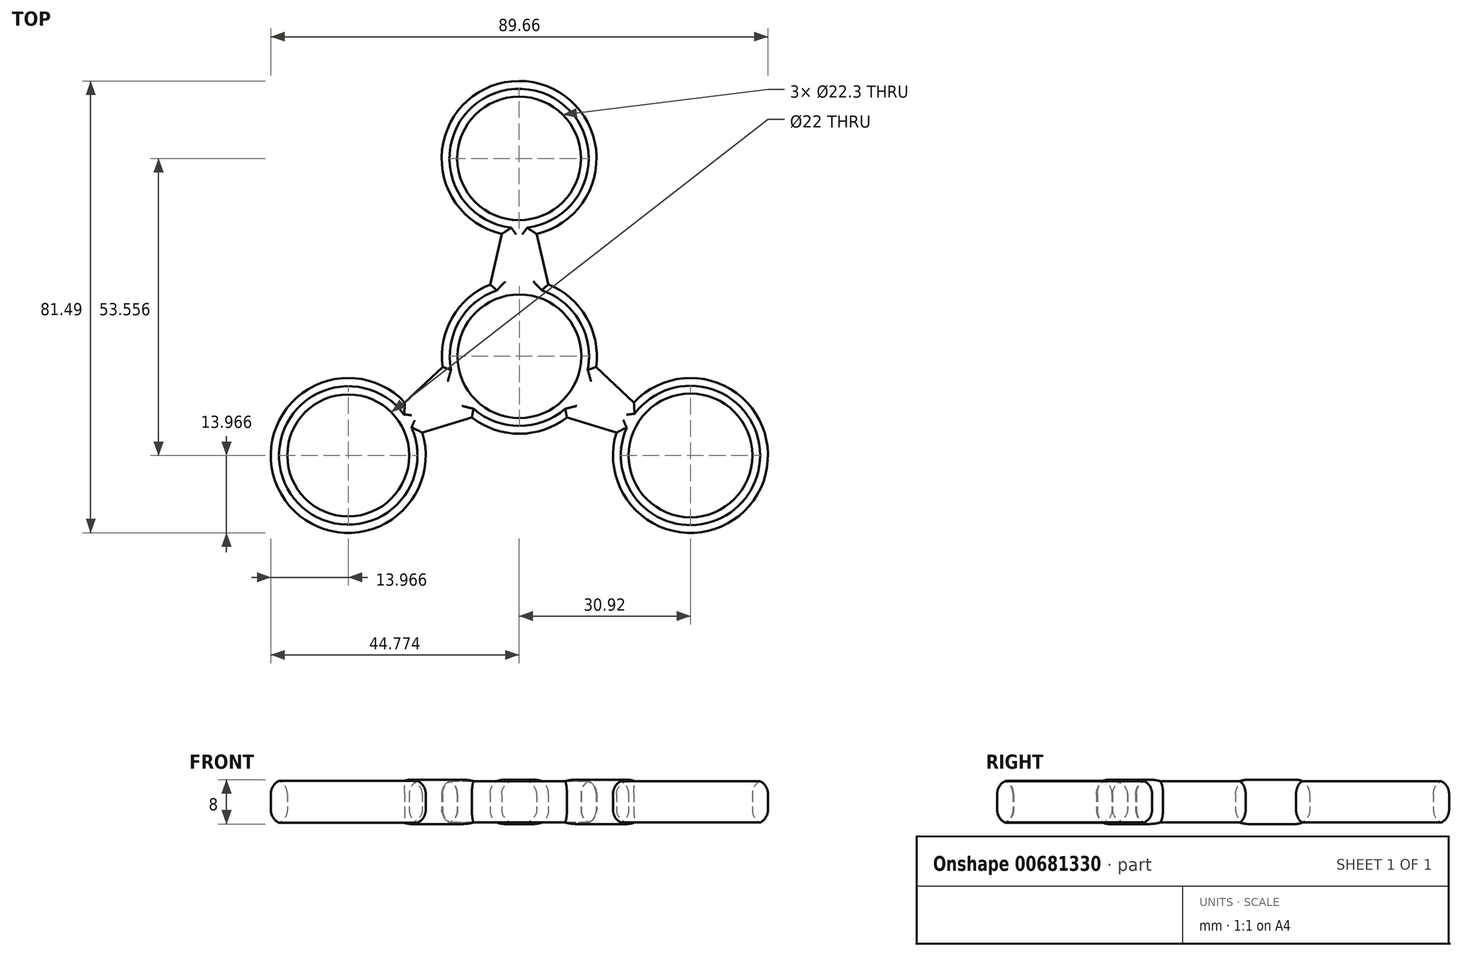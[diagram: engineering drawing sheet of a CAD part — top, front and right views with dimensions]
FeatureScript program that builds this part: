
annotation { "Feature Type Name" : "Feature", "Feature Type Description" : "" }
export const myFeature = defineFeature(function(context is Context, id is Id, definition is map)
    precondition{}
    {
        {
            var Q0;
            Q0=qCreatedBy(makeId("Top.planeOp"),FACE);
            var sketch = newSketch(context, id + "F0", { "sketchPlane" : qUnion([Q0])});
            skPoint(sketch, "E0.0.midPoint", {"position": v(30.86, 17.88) * mm});
            skLineSegment(sketch, "E1", {"start": v(0, 0) * mm, "end": v(-0.11, 71.34) * mm});
            skLineSegment(sketch, "E2", {"start": v(0, 0) * mm, "end": v(61.84, -35.57) * mm});
            skLineSegment(sketch, "E3", {"start": v(0, 0) * mm, "end": v(-61.73, -35.77) * mm});
            skCircle(sketch, "E4", {"center": v(-0.06, 35.67) * mm, "radius": 11.15 * mm});
            skCircle(sketch, "E5", {"center": v(30.86, -17.88) * mm, "radius": 11.15 * mm});
            skCircle(sketch, "E6", {"center": v(-30.86, -17.88) * mm, "radius": 11 * mm});
            skLineSegment(sketch, "E7", {"start": v(-30.86, -17.88) * mm, "end": v(0, -8.4) * mm});
            skLineSegment(sketch, "E8", {"start": v(0, -8.4) * mm, "end": v(30.86, -17.88) * mm});
            skLineSegment(sketch, "E9", {"start": v(0, 0) * mm, "end": v(7.27, 4.22) * mm});
            skLineSegment(sketch, "E10", {"start": v(0, -8.4) * mm, "end": v(0, 0) * mm});
            skLineSegment(sketch, "E11", {"start": v(-0.06, 35.67) * mm, "end": v(7.27, 4.22) * mm});
            skLineSegment(sketch, "E12", {"start": v(7.27, 4.22) * mm, "end": v(30.86, -17.88) * mm});
            skLineSegment(sketch, "E13", {"start": v(0, 0) * mm, "end": v(-7.29, 4.2) * mm});
            skLineSegment(sketch, "E14", {"start": v(-0.06, 35.67) * mm, "end": v(-7.29, 4.2) * mm});
            skLineSegment(sketch, "E15", {"start": v(-7.29, 4.2) * mm, "end": v(-30.86, -17.88) * mm});
            skCircle(sketch, "E16", {"center": v(0, 0) * mm, "radius": 11.15 * mm});
            skCircle(sketch, "E17", {"center": v(-30.86, -17.88) * mm, "radius": 13.97 * mm});
            skCircle(sketch, "E18", {"center": v(30.86, -17.88) * mm, "radius": 13.97 * mm});
            skCircle(sketch, "E19", {"center": v(-0.06, 35.67) * mm, "radius": 13.97 * mm});
            skCircle(sketch, "E20", {"center": v(0, 0) * mm, "radius": 13.97 * mm});
            skSolve(sketch);
        }
        {
            var Q0;
            {var subQ0=sQuery(id+"F0.wireOp",EDGE,"E19");var subQ1=sQuery(id+"F0.wireOp",EDGE,"E1");var subQ2=makeQuery(id+"F0.imprint","INTERSECT",VERTEX,{"disambiguationData":[OD(0.0)],"derivedFrom":[subQ1,subQ0]});Q0=makeQuery(id+"F0.imprint","IMPRINT",FACE,{"disambiguationData":[TD([[makeQuery(id+"F0.imprint","IMPRINT",EDGE,{"disambiguationData":[TD([[subQ2,1.0]])],"derivedFrom":subQ1}),-1.0]])]});}
            var Q1;
            {var subQ0=sQuery(id+"F0.wireOp",EDGE,"E19");var subQ1=sQuery(id+"F0.wireOp",EDGE,"E1");var subQ2=makeQuery(id+"F0.imprint","INTERSECT",VERTEX,{"disambiguationData":[OD(0.0)],"derivedFrom":[subQ1,subQ0]});Q1=makeQuery(id+"F0.imprint","IMPRINT",FACE,{"disambiguationData":[TD([[makeQuery(id+"F0.imprint","IMPRINT",EDGE,{"disambiguationData":[TD([[subQ2,1.0]])],"derivedFrom":subQ1}),1.0]])]});}
            var Q2;
            {var subQ0=sQuery(id+"F0.wireOp",EDGE,"E20");var subQ1=sQuery(id+"F0.wireOp",EDGE,"E1");var subQ2=makeQuery(id+"F0.imprint","INTERSECT",VERTEX,{"derivedFrom":[subQ1,subQ0]});Q2=makeQuery(id+"F0.imprint","IMPRINT",FACE,{"disambiguationData":[TD([[makeQuery(id+"F0.imprint","IMPRINT",EDGE,{"disambiguationData":[TD([[subQ2,-1.0]])],"derivedFrom":subQ1}),1.0]])]});}
            var Q3;
            {var subQ0=sQuery(id+"F0.wireOp",EDGE,"E20");var subQ1=sQuery(id+"F0.wireOp",EDGE,"E1");var subQ2=makeQuery(id+"F0.imprint","INTERSECT",VERTEX,{"derivedFrom":[subQ1,subQ0]});Q3=makeQuery(id+"F0.imprint","IMPRINT",FACE,{"disambiguationData":[TD([[makeQuery(id+"F0.imprint","IMPRINT",EDGE,{"disambiguationData":[TD([[subQ2,-1.0]])],"derivedFrom":subQ1}),-1.0]])]});}
            var Q4;
            {var subQ0=sQuery(id+"F0.wireOp",EDGE,"E19");var subQ1=sQuery(id+"F0.wireOp",EDGE,"E1");var subQ2=makeQuery(id+"F0.imprint","INTERSECT",VERTEX,{"disambiguationData":[OD(1.0)],"derivedFrom":[subQ1,subQ0]});Q4=makeQuery(id+"F0.imprint","IMPRINT",FACE,{"disambiguationData":[TD([[makeQuery(id+"F0.imprint","IMPRINT",EDGE,{"disambiguationData":[TD([[subQ2,-1.0]])],"derivedFrom":subQ1}),-1.0]])]});}
            var Q5;
            {var subQ0=sQuery(id+"F0.wireOp",EDGE,"E19");var subQ1=sQuery(id+"F0.wireOp",EDGE,"E1");var subQ2=makeQuery(id+"F0.imprint","INTERSECT",VERTEX,{"disambiguationData":[OD(1.0)],"derivedFrom":[subQ1,subQ0]});Q5=makeQuery(id+"F0.imprint","IMPRINT",FACE,{"disambiguationData":[TD([[makeQuery(id+"F0.imprint","IMPRINT",EDGE,{"disambiguationData":[TD([[subQ2,-1.0]])],"derivedFrom":subQ1}),1.0]])]});}
            var Q6;
            {var subQ0=sQuery(id+"F0.wireOp",EDGE,"E20");var subQ1=sQuery(id+"F0.wireOp",EDGE,"E11");var subQ2=makeQuery(id+"F0.imprint","INTERSECT",VERTEX,{"derivedFrom":[subQ1,subQ0]});Q6=makeQuery(id+"F0.imprint","IMPRINT",FACE,{"disambiguationData":[TD([[makeQuery(id+"F0.imprint","IMPRINT",EDGE,{"disambiguationData":[TD([[subQ2,-1.0]])],"derivedFrom":subQ1}),1.0]])]});}
            var Q7;
            {var subQ0=sQuery(id+"F0.wireOp",EDGE,"E20");var subQ1=sQuery(id+"F0.wireOp",EDGE,"E14");var subQ2=makeQuery(id+"F0.imprint","INTERSECT",VERTEX,{"derivedFrom":[subQ1,subQ0]});Q7=makeQuery(id+"F0.imprint","IMPRINT",FACE,{"disambiguationData":[TD([[makeQuery(id+"F0.imprint","IMPRINT",EDGE,{"disambiguationData":[TD([[subQ2,-1.0]])],"derivedFrom":subQ1}),-1.0]])]});}
            var Q8;
            {var subQ0=sQuery(id+"F0.wireOp",EDGE,"E16");var subQ1=sQuery(id+"F0.wireOp",EDGE,"E1");var subQ2=makeQuery(id+"F0.imprint","INTERSECT",VERTEX,{"derivedFrom":[subQ1,subQ0]});Q8=makeQuery(id+"F0.imprint","IMPRINT",FACE,{"disambiguationData":[TD([[makeQuery(id+"F0.imprint","IMPRINT",EDGE,{"disambiguationData":[TD([[subQ2,-1.0]])],"derivedFrom":subQ1}),-1.0]])]});}
            var Q9;
            {var subQ0=sQuery(id+"F0.wireOp",EDGE,"E16");var subQ1=sQuery(id+"F0.wireOp",EDGE,"E1");var subQ2=makeQuery(id+"F0.imprint","INTERSECT",VERTEX,{"derivedFrom":[subQ1,subQ0]});Q9=makeQuery(id+"F0.imprint","IMPRINT",FACE,{"disambiguationData":[TD([[makeQuery(id+"F0.imprint","IMPRINT",EDGE,{"disambiguationData":[TD([[subQ2,-1.0]])],"derivedFrom":subQ1}),1.0]])]});}
            var Q10;
            {var subQ0=sQuery(id+"F0.wireOp",EDGE,"E16");var subQ1=sQuery(id+"F0.wireOp",EDGE,"E3");var subQ2=makeQuery(id+"F0.imprint","INTERSECT",VERTEX,{"derivedFrom":[subQ1,subQ0]});Q10=makeQuery(id+"F0.imprint","IMPRINT",FACE,{"disambiguationData":[TD([[makeQuery(id+"F0.imprint","IMPRINT",EDGE,{"disambiguationData":[TD([[subQ2,-1.0]])],"derivedFrom":subQ1}),1.0]])]});}
            var Q11;
            {var subQ0=sQuery(id+"F0.wireOp",EDGE,"E20");var subQ1=sQuery(id+"F0.wireOp",EDGE,"E7");var subQ2=makeQuery(id+"F0.imprint","INTERSECT",VERTEX,{"derivedFrom":[subQ1,subQ0]});Q11=makeQuery(id+"F0.imprint","IMPRINT",FACE,{"disambiguationData":[TD([[makeQuery(id+"F0.imprint","IMPRINT",EDGE,{"disambiguationData":[TD([[subQ2,-1.0]])],"derivedFrom":subQ1}),-1.0]])]});}
            var Q12;
            {var subQ0=sQuery(id+"F0.wireOp",EDGE,"E16");var subQ1=sQuery(id+"F0.wireOp",EDGE,"E2");var subQ2=makeQuery(id+"F0.imprint","INTERSECT",VERTEX,{"derivedFrom":[subQ1,subQ0]});Q12=makeQuery(id+"F0.imprint","IMPRINT",FACE,{"disambiguationData":[TD([[makeQuery(id+"F0.imprint","IMPRINT",EDGE,{"disambiguationData":[TD([[subQ2,-1.0]])],"derivedFrom":subQ1}),1.0]])]});}
            var Q13;
            {var subQ0=sQuery(id+"F0.wireOp",EDGE,"E16");var subQ1=sQuery(id+"F0.wireOp",EDGE,"E2");var subQ2=makeQuery(id+"F0.imprint","INTERSECT",VERTEX,{"derivedFrom":[subQ1,subQ0]});Q13=makeQuery(id+"F0.imprint","IMPRINT",FACE,{"disambiguationData":[TD([[makeQuery(id+"F0.imprint","IMPRINT",EDGE,{"disambiguationData":[TD([[subQ2,-1.0]])],"derivedFrom":subQ1}),-1.0]])]});}
            var Q14;
            {var subQ0=sQuery(id+"F0.wireOp",EDGE,"E16");var subQ1=sQuery(id+"F0.wireOp",EDGE,"E3");var subQ2=makeQuery(id+"F0.imprint","INTERSECT",VERTEX,{"derivedFrom":[subQ1,subQ0]});Q14=makeQuery(id+"F0.imprint","IMPRINT",FACE,{"disambiguationData":[TD([[makeQuery(id+"F0.imprint","IMPRINT",EDGE,{"disambiguationData":[TD([[subQ2,-1.0]])],"derivedFrom":subQ1}),-1.0]])]});}
            var Q15;
            {var subQ0=sQuery(id+"F0.wireOp",EDGE,"E20");var subQ1=sQuery(id+"F0.wireOp",EDGE,"E2");var subQ2=makeQuery(id+"F0.imprint","INTERSECT",VERTEX,{"derivedFrom":[subQ1,subQ0]});Q15=makeQuery(id+"F0.imprint","IMPRINT",FACE,{"disambiguationData":[TD([[makeQuery(id+"F0.imprint","IMPRINT",EDGE,{"disambiguationData":[TD([[subQ2,-1.0]])],"derivedFrom":subQ1}),-1.0]])]});}
            var Q16;
            {var subQ0=sQuery(id+"F0.wireOp",EDGE,"E20");var subQ1=sQuery(id+"F0.wireOp",EDGE,"E2");var subQ2=makeQuery(id+"F0.imprint","INTERSECT",VERTEX,{"derivedFrom":[subQ1,subQ0]});Q16=makeQuery(id+"F0.imprint","IMPRINT",FACE,{"disambiguationData":[TD([[makeQuery(id+"F0.imprint","IMPRINT",EDGE,{"disambiguationData":[TD([[subQ2,-1.0]])],"derivedFrom":subQ1}),1.0]])]});}
            var Q17;
            {var subQ0=sQuery(id+"F0.wireOp",EDGE,"E20");var subQ1=sQuery(id+"F0.wireOp",EDGE,"E3");var subQ2=makeQuery(id+"F0.imprint","INTERSECT",VERTEX,{"derivedFrom":[subQ1,subQ0]});Q17=makeQuery(id+"F0.imprint","IMPRINT",FACE,{"disambiguationData":[TD([[makeQuery(id+"F0.imprint","IMPRINT",EDGE,{"disambiguationData":[TD([[subQ2,-1.0]])],"derivedFrom":subQ1}),-1.0]])]});}
            var Q18;
            {var subQ0=sQuery(id+"F0.wireOp",EDGE,"E20");var subQ1=sQuery(id+"F0.wireOp",EDGE,"E3");var subQ2=makeQuery(id+"F0.imprint","INTERSECT",VERTEX,{"derivedFrom":[subQ1,subQ0]});Q18=makeQuery(id+"F0.imprint","IMPRINT",FACE,{"disambiguationData":[TD([[makeQuery(id+"F0.imprint","IMPRINT",EDGE,{"disambiguationData":[TD([[subQ2,-1.0]])],"derivedFrom":subQ1}),1.0]])]});}
            var Q19;
            {var subQ0=sQuery(id+"F0.wireOp",EDGE,"E17");var subQ1=sQuery(id+"F0.wireOp",EDGE,"E3");var subQ2=makeQuery(id+"F0.imprint","INTERSECT",VERTEX,{"disambiguationData":[OD(0.0)],"derivedFrom":[subQ1,subQ0]});Q19=makeQuery(id+"F0.imprint","IMPRINT",FACE,{"disambiguationData":[TD([[makeQuery(id+"F0.imprint","IMPRINT",EDGE,{"disambiguationData":[TD([[subQ2,1.0]])],"derivedFrom":subQ1}),-1.0]])]});}
            var Q20;
            {var subQ0=sQuery(id+"F0.wireOp",EDGE,"E17");var subQ1=sQuery(id+"F0.wireOp",EDGE,"E3");var subQ2=makeQuery(id+"F0.imprint","INTERSECT",VERTEX,{"disambiguationData":[OD(1.0)],"derivedFrom":[subQ1,subQ0]});Q20=makeQuery(id+"F0.imprint","IMPRINT",FACE,{"disambiguationData":[TD([[makeQuery(id+"F0.imprint","IMPRINT",EDGE,{"disambiguationData":[TD([[subQ2,-1.0]])],"derivedFrom":subQ1}),1.0]])]});}
            var Q21;
            {var subQ0=sQuery(id+"F0.wireOp",EDGE,"E17");var subQ1=sQuery(id+"F0.wireOp",EDGE,"E3");var subQ2=makeQuery(id+"F0.imprint","INTERSECT",VERTEX,{"disambiguationData":[OD(1.0)],"derivedFrom":[subQ1,subQ0]});Q21=makeQuery(id+"F0.imprint","IMPRINT",FACE,{"disambiguationData":[TD([[makeQuery(id+"F0.imprint","IMPRINT",EDGE,{"disambiguationData":[TD([[subQ2,-1.0]])],"derivedFrom":subQ1}),-1.0]])]});}
            var Q22;
            {var subQ0=sQuery(id+"F0.wireOp",EDGE,"E17");var subQ1=sQuery(id+"F0.wireOp",EDGE,"E3");var subQ2=makeQuery(id+"F0.imprint","INTERSECT",VERTEX,{"disambiguationData":[OD(0.0)],"derivedFrom":[subQ1,subQ0]});Q22=makeQuery(id+"F0.imprint","IMPRINT",FACE,{"disambiguationData":[TD([[makeQuery(id+"F0.imprint","IMPRINT",EDGE,{"disambiguationData":[TD([[subQ2,1.0]])],"derivedFrom":subQ1}),1.0]])]});}
            var Q23;
            {var subQ0=sQuery(id+"F0.wireOp",EDGE,"E18");var subQ1=sQuery(id+"F0.wireOp",EDGE,"E2");var subQ2=makeQuery(id+"F0.imprint","INTERSECT",VERTEX,{"disambiguationData":[OD(1.0)],"derivedFrom":[subQ1,subQ0]});Q23=makeQuery(id+"F0.imprint","IMPRINT",FACE,{"disambiguationData":[TD([[makeQuery(id+"F0.imprint","IMPRINT",EDGE,{"disambiguationData":[TD([[subQ2,-1.0]])],"derivedFrom":subQ1}),1.0]])]});}
            var Q24;
            {var subQ0=sQuery(id+"F0.wireOp",EDGE,"E18");var subQ1=sQuery(id+"F0.wireOp",EDGE,"E2");var subQ2=makeQuery(id+"F0.imprint","INTERSECT",VERTEX,{"disambiguationData":[OD(1.0)],"derivedFrom":[subQ1,subQ0]});Q24=makeQuery(id+"F0.imprint","IMPRINT",FACE,{"disambiguationData":[TD([[makeQuery(id+"F0.imprint","IMPRINT",EDGE,{"disambiguationData":[TD([[subQ2,-1.0]])],"derivedFrom":subQ1}),-1.0]])]});}
            var Q25;
            {var subQ0=sQuery(id+"F0.wireOp",EDGE,"E18");var subQ1=sQuery(id+"F0.wireOp",EDGE,"E2");var subQ2=makeQuery(id+"F0.imprint","INTERSECT",VERTEX,{"disambiguationData":[OD(0.0)],"derivedFrom":[subQ1,subQ0]});Q25=makeQuery(id+"F0.imprint","IMPRINT",FACE,{"disambiguationData":[TD([[makeQuery(id+"F0.imprint","IMPRINT",EDGE,{"disambiguationData":[TD([[subQ2,1.0]])],"derivedFrom":subQ1}),-1.0]])]});}
            var Q26;
            {var subQ0=sQuery(id+"F0.wireOp",EDGE,"E18");var subQ1=sQuery(id+"F0.wireOp",EDGE,"E2");var subQ2=makeQuery(id+"F0.imprint","INTERSECT",VERTEX,{"disambiguationData":[OD(0.0)],"derivedFrom":[subQ1,subQ0]});Q26=makeQuery(id+"F0.imprint","IMPRINT",FACE,{"disambiguationData":[TD([[makeQuery(id+"F0.imprint","IMPRINT",EDGE,{"disambiguationData":[TD([[subQ2,1.0]])],"derivedFrom":subQ1}),1.0]])]});}
            extrude(context, id + "F1", {"entities" : qUnion([Q0, Q1, Q2, Q3, Q4, Q5, Q6, Q7, Q8, Q9, Q10, Q11, Q12, Q13, Q14, Q15, Q16, Q17, Q18, Q19, Q20, Q21, Q22, Q23, Q24, Q25, Q26]), "depth" : 8 * mm, "offsetDistance" : 25.4 * mm});
        }
        {
            var Q0;
            Q0=makeQuery(id+"F1.opExtrude","CAP_FACE",FACE,{"disambiguationData":[OSD([sQuery(id+"F0.wireOp",EDGE,"E4"),sQuery(id+"F0.wireOp",EDGE,"E5"),sQuery(id+"F0.wireOp",EDGE,"E6"),sQuery(id+"F0.wireOp",EDGE,"E7"),sQuery(id+"F0.wireOp",EDGE,"E8"),sQuery(id+"F0.wireOp",EDGE,"E11"),sQuery(id+"F0.wireOp",EDGE,"E12"),sQuery(id+"F0.wireOp",EDGE,"E14"),sQuery(id+"F0.wireOp",EDGE,"E15"),sQuery(id+"F0.wireOp",EDGE,"E16"),sQuery(id+"F0.wireOp",EDGE,"E17"),sQuery(id+"F0.wireOp",EDGE,"E18"),sQuery(id+"F0.wireOp",EDGE,"E19"),sQuery(id+"F0.wireOp",EDGE,"E20")])],"isStart":false});
            var Q1;
            Q1=makeQuery(id+"F1.opExtrude","CAP_FACE",FACE,{"disambiguationData":[OSD([sQuery(id+"F0.wireOp",EDGE,"E4"),sQuery(id+"F0.wireOp",EDGE,"E5"),sQuery(id+"F0.wireOp",EDGE,"E6"),sQuery(id+"F0.wireOp",EDGE,"E7"),sQuery(id+"F0.wireOp",EDGE,"E8"),sQuery(id+"F0.wireOp",EDGE,"E11"),sQuery(id+"F0.wireOp",EDGE,"E12"),sQuery(id+"F0.wireOp",EDGE,"E14"),sQuery(id+"F0.wireOp",EDGE,"E15"),sQuery(id+"F0.wireOp",EDGE,"E16"),sQuery(id+"F0.wireOp",EDGE,"E17"),sQuery(id+"F0.wireOp",EDGE,"E18"),sQuery(id+"F0.wireOp",EDGE,"E19"),sQuery(id+"F0.wireOp",EDGE,"E20")])],"isStart":true});
            fillet(context, id + "F2", {"entities" : qUnion([Q0, Q1]), "radius" : 2.54 * mm, "tangentPropagation" : true, "allowEdgeOverflow" : false});
        }
    });
